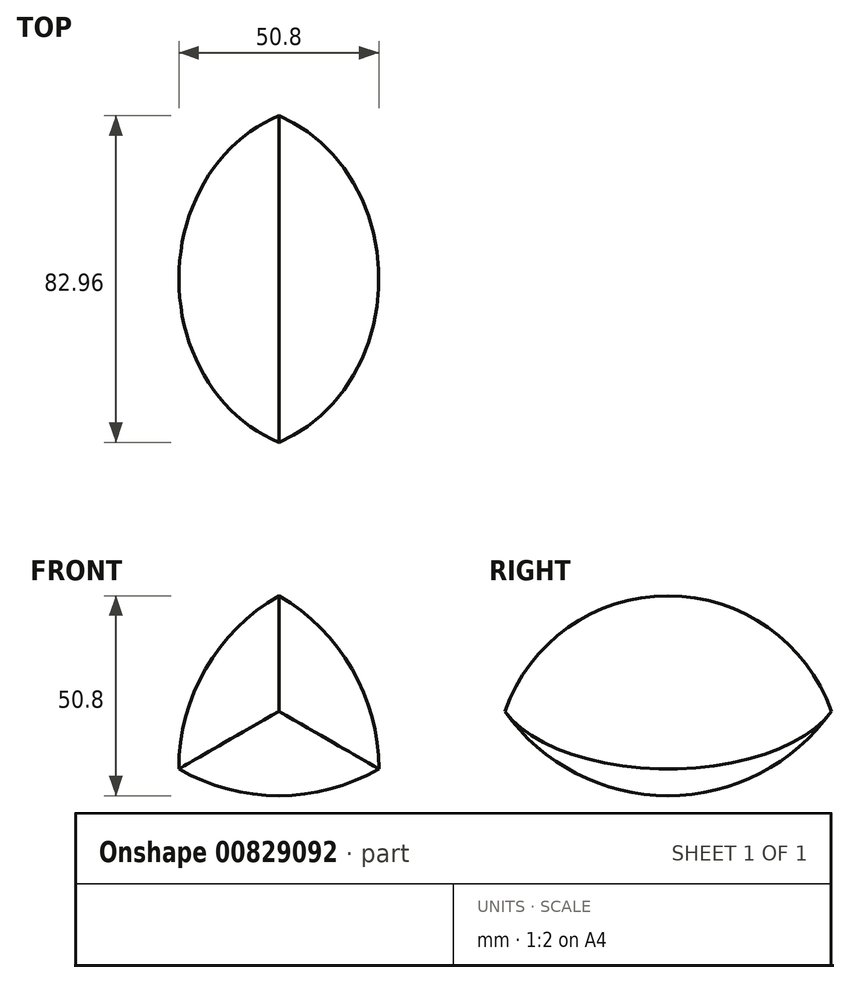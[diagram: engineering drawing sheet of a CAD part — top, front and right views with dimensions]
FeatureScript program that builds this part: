
annotation { "Feature Type Name" : "Feature", "Feature Type Description" : "" }
export const myFeature = defineFeature(function(context is Context, id is Id, definition is map)
    precondition{}
    {
        {
            var Q0;
            Q0=qCreatedBy(makeId("Front.planeOp"),FACE);
            var sketch = newSketch(context, id + "F0", { "sketchPlane" : qUnion([Q0])});
            skLineSegment(sketch, "E0", {"start": v(0, 0) * mm, "end": v(50.8, 0) * mm, "construction": true});
            skLineSegment(sketch, "E1", {"start": v(50.8, 0) * mm, "end": v(25.4, 44) * mm, "construction": true});
            skLineSegment(sketch, "E2", {"start": v(25.4, 44) * mm, "end": v(0, 0) * mm, "construction": true});
            skPoint(sketch, "E3", {"position": v(25.4, 0) * mm});
            skPoint(sketch, "E4", {"position": v(38.1, 22) * mm});
            skPoint(sketch, "E5", {"position": v(12.7, 22) * mm});
            skPoint(sketch, "E6", {"position": v(25.4, 22) * mm});
            skPoint(sketch, "E7", {"position": v(25.4, 14.66) * mm});
            skLineSegment(sketch, "E8", {"start": v(25.4, 0) * mm, "end": v(25.4, 14.66) * mm, "construction": true});
            skLineSegment(sketch, "E9", {"start": v(12.7, 22) * mm, "end": v(25.4, 14.66) * mm, "construction": true});
            skLineSegment(sketch, "E10", {"start": v(38.1, 22) * mm, "end": v(25.4, 14.66) * mm, "construction": true});
            skSolve(sketch);
        }
        {
            var Q0;
            Q0=qCreatedBy(makeId("Front.planeOp"),FACE);
            var sketch = newSketch(context, id + "F1", { "sketchPlane" : qUnion([Q0])});
            skCircle(sketch, "E11", {"center": v(0, 0) * mm, "radius": 50.8 * mm});
            skLineSegment(sketch, "E12", {"start": v(0, 0) * mm, "end": v(25.43, 43.97) * mm});
            skLineSegment(sketch, "E13", {"start": v(0, 0) * mm, "end": v(-25.43, -43.97) * mm});
            skSolve(sketch);
        }
        {
            var Q0;
            {var subQ0=sQuery(id+"F1.wireOp",EDGE,"E12");Q0=makeQuery(id+"F1.imprint","IMPRINT",FACE,{"disambiguationData":[TD([[makeQuery(id+"F1.imprint","IMPRINT",EDGE,{"derivedFrom":subQ0}),1.0]])]});}
            var Q1;
            Q1=sQuery(id+"F1.wireOp",EDGE,"E12");
            revolve(context, id + "F2", {"surfaceOperationType" : NewSurfaceOperationType.NEW, "entities" : qUnion([Q0]), "axis" : qUnion([Q1]), "revolveType" : RevolveType.FULL});
        }
        {
            var Q0;
            Q0=qCreatedBy(makeId("Front.planeOp"),FACE);
            var sketch = newSketch(context, id + "F3", { "sketchPlane" : qUnion([Q0])});
            skPoint(sketch, "E14", {"position": v(50.8, 0) * mm});
            skCircle(sketch, "E15", {"center": v(50.8, 0) * mm, "radius": 50.8 * mm});
            skLineSegment(sketch, "E16", {"start": v(50.8, 0) * mm, "end": v(0, 0) * mm});
            skLineSegment(sketch, "E17", {"start": v(50.8, 0) * mm, "end": v(101.6, 0) * mm});
            skSolve(sketch);
        }
        {
            var Q0;
            {var subQ0=sQuery(id+"F3.wireOp",EDGE,"E16");Q0=makeQuery(id+"F3.imprint","IMPRINT",FACE,{"disambiguationData":[TD([[makeQuery(id+"F3.imprint","IMPRINT",EDGE,{"derivedFrom":subQ0}),-1.0]])]});}
            var Q1;
            Q1=sQuery(id+"F3.wireOp",EDGE,"E17");
            revolve(context, id + "F4", {"operationType" : NewBodyOperationType.INTERSECT, "surfaceOperationType" : NewSurfaceOperationType.NEW, "entities" : qUnion([Q0]), "axis" : qUnion([Q1]), "revolveType" : RevolveType.FULL});
        }
        {
            var Q0;
            Q0=qCreatedBy(makeId("Front.planeOp"),FACE);
            var sketch = newSketch(context, id + "F5", { "sketchPlane" : qUnion([Q0])});
            skPoint(sketch, "E18", {"position": v(50.8, 0) * mm});
            skPoint(sketch, "E19", {"position": v(25.4, 44) * mm});
            skCircle(sketch, "E20", {"center": v(25.4, 44) * mm, "radius": 50.8 * mm});
            skLineSegment(sketch, "E21", {"start": v(25.4, 44) * mm, "end": v(0, 0) * mm});
            skLineSegment(sketch, "E22", {"start": v(25.4, 44) * mm, "end": v(50.8, 87.99) * mm});
            skSolve(sketch);
        }
        {
            var Q0;
            {var subQ0=sQuery(id+"F5.wireOp",EDGE,"E21");Q0=makeQuery(id+"F5.imprint","IMPRINT",FACE,{"disambiguationData":[TD([[makeQuery(id+"F5.imprint","IMPRINT",EDGE,{"derivedFrom":subQ0}),-1.0]])]});}
            var Q1;
            Q1=sQuery(id+"F5.wireOp",EDGE,"E21");
            revolve(context, id + "F6", {"operationType" : NewBodyOperationType.INTERSECT, "surfaceOperationType" : NewSurfaceOperationType.NEW, "entities" : qUnion([Q0]), "axis" : qUnion([Q1]), "revolveType" : RevolveType.FULL});
        }
        {
            var Q0;
            Q0=qCreatedBy(makeId("Front.planeOp"),FACE);
            cPlane(context, id + "F7", {"entities" : qUnion([Q0]), "cplaneType" : CPlaneType.OFFSET, "offset" : (sqrt(3)) * mm, "width" : 152.4 * mm, "height" : 152.4 * mm});
        }
        {
            var Q0;
            Q0=qCreatedBy(id+"F7.planeOp",FACE);
            var sketch = newSketch(context, id + "F8", { "sketchPlane" : qUnion([Q0])});
            skPoint(sketch, "E23", {"position": v(50.8, 0) * mm});
            skPoint(sketch, "E24", {"position": v(25.4, 44) * mm});
            skPoint(sketch, "E25", {"position": v(25.4, 14.66) * mm});
            skLineSegment(sketch, "E26", {"start": v(25.4, 44) * mm, "end": v(25.4, 14.66) * mm, "construction": true});
            skLineSegment(sketch, "E27", {"start": v(50.8, 0) * mm, "end": v(25.4, 14.66) * mm, "construction": true});
            skLineSegment(sketch, "E28", {"start": v(0, 0) * mm, "end": v(25.4, 14.66) * mm, "construction": true});
            skCircle(sketch, "E29", {"center": v(25.4, 14.66) * mm, "radius": 50.8 * mm});
            skLineSegment(sketch, "E30", {"start": v(25.4, 14.66) * mm, "end": v(-25.4, 14.66) * mm});
            skLineSegment(sketch, "E31", {"start": v(25.4, 14.66) * mm, "end": v(76.2, 14.66) * mm});
            skSolve(sketch);
        }
        {
            var Q0;
            {var subQ0=sQuery(id+"F8.wireOp",EDGE,"E30");Q0=makeQuery(id+"F8.imprint","IMPRINT",FACE,{"disambiguationData":[TD([[makeQuery(id+"F8.imprint","IMPRINT",EDGE,{"derivedFrom":subQ0}),-1.0]])]});}
            var Q1;
            Q1=sQuery(id+"F8.wireOp",EDGE,"E30");
            revolve(context, id + "F9", {"operationType" : NewBodyOperationType.INTERSECT, "surfaceOperationType" : NewSurfaceOperationType.NEW, "entities" : qUnion([Q0]), "axis" : qUnion([Q1]), "revolveType" : RevolveType.FULL});
        }
    });
